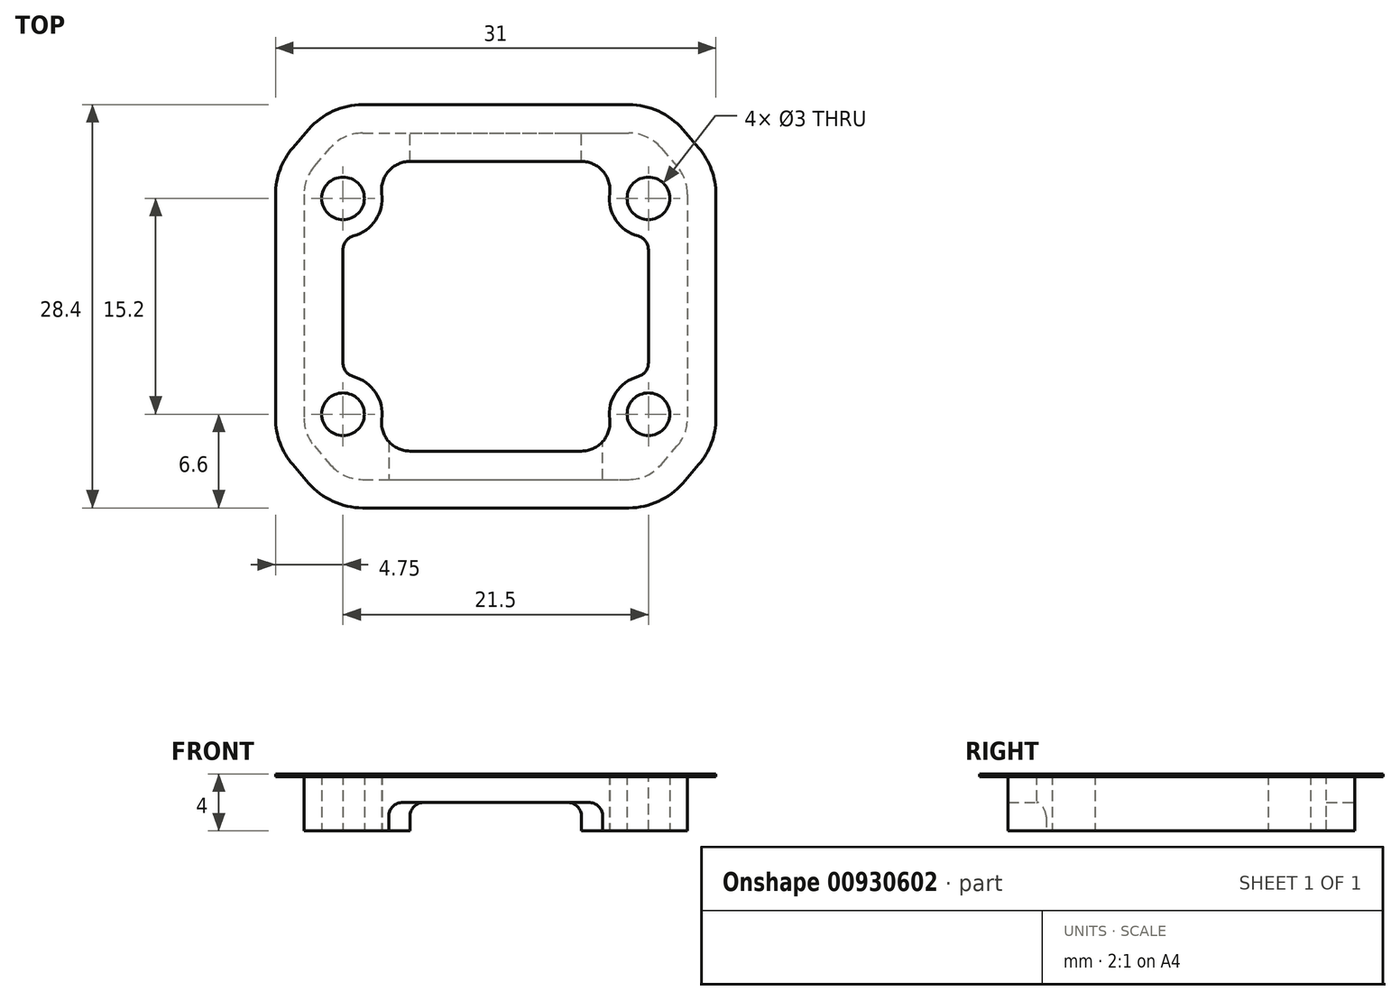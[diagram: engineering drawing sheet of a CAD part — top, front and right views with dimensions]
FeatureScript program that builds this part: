
annotation { "Feature Type Name" : "Feature", "Feature Type Description" : "" }
export const myFeature = defineFeature(function(context is Context, id is Id, definition is map)
    precondition{}
    {
        {
            var Q0;
            Q0=qCreatedBy(makeId("Top.planeOp"),FACE);
            var sketch = newSketch(context, id + "F0", { "sketchPlane" : qUnion([Q0])});
            skCircle(sketch, "E0", {"center": v(0, 0) * mm, "radius": 1.5 * mm});
            skCircle(sketch, "E1", {"center": v(0, 15.2) * mm, "radius": 1.5 * mm});
            skCircle(sketch, "E2", {"center": v(21.5, 15.2) * mm, "radius": 1.5 * mm});
            skCircle(sketch, "E3", {"center": v(21.5, 0) * mm, "radius": 1.5 * mm});
            skLineSegment(sketch, "E4", {"start": v(-2.75, 16.6) * mm, "end": v(-2.75, -1.4) * mm});
            skLineSegment(sketch, "E5", {"start": v(24.25, 16.6) * mm, "end": v(24.25, -1.4) * mm});
            skLineSegment(sketch, "E6", {"start": v(0.9, -2.6) * mm, "end": v(20.6, -2.6) * mm});
            skLineSegment(sketch, "E7", {"start": v(0.9, 17.8) * mm, "end": v(20.6, 17.8) * mm});
            skArc(sketch, "E8", {"start": v(0, 12.45) * mm, "mid": v(2.71, 14.75) * mm, "end": v(0.9, 17.8) * mm});
            skLineSegment(sketch, "E9", {"start": v(0, 12.45) * mm, "end": v(0, 2.75) * mm});
            skLineSegment(sketch, "E10", {"start": v(0, 19.8) * mm, "end": v(21.5, 19.8) * mm});
            skLineSegment(sketch, "E11", {"start": v(-2.75, 16.6) * mm, "end": v(0, 19.8) * mm});
            skLineSegment(sketch, "E12", {"start": v(21.5, 12.45) * mm, "end": v(21.5, 2.75) * mm});
            skArc(sketch, "E13", {"start": v(20.6, 17.8) * mm, "mid": v(18.79, 14.75) * mm, "end": v(21.5, 12.45) * mm});
            skLineSegment(sketch, "E14", {"start": v(21.5, 19.8) * mm, "end": v(24.25, 16.6) * mm});
            skLineSegment(sketch, "E15", {"start": v(0, -4.6) * mm, "end": v(21.5, -4.6) * mm});
            skLineSegment(sketch, "E16", {"start": v(21.5, -4.6) * mm, "end": v(24.25, -1.4) * mm});
            skLineSegment(sketch, "E17", {"start": v(-2.75, -1.4) * mm, "end": v(0, -4.6) * mm});
            skArc(sketch, "E18", {"start": v(0.9, -2.6) * mm, "mid": v(2.71, 0.45) * mm, "end": v(0, 2.75) * mm});
            skArc(sketch, "E19", {"start": v(21.5, 2.75) * mm, "mid": v(18.79, 0.45) * mm, "end": v(20.6, -2.6) * mm});
            skSolve(sketch);
        }
        {
            var Q0;
            Q0=qSketchRegion(id+"F0",true);
            extrude(context, id + "F1", {"entities" : qUnion([Q0]), "depth" : 4 * mm, "offsetDistance" : 25 * mm});
        }
        {
            var Q0;
            Q0=makeQuery(id+"F1.opExtrude","SWEPT_EDGE",EDGE,{"disambiguationData":[OSD([sQuery(id+"F0.wireOp",EDGE,"E7"),sQuery(id+"F0.wireOp",EDGE,"E8")])]});
            var Q1;
            Q1=makeQuery(id+"F1.opExtrude","SWEPT_EDGE",EDGE,{"disambiguationData":[OSD([sQuery(id+"F0.wireOp",EDGE,"E7"),sQuery(id+"F0.wireOp",EDGE,"E13")])]});
            var Q2;
            Q2=makeQuery(id+"F1.opExtrude","SWEPT_EDGE",EDGE,{"disambiguationData":[OSD([sQuery(id+"F0.wireOp",EDGE,"E6"),sQuery(id+"F0.wireOp",EDGE,"E18")])]});
            var Q3;
            Q3=makeQuery(id+"F1.opExtrude","SWEPT_EDGE",EDGE,{"disambiguationData":[OSD([sQuery(id+"F0.wireOp",EDGE,"E6"),sQuery(id+"F0.wireOp",EDGE,"E19")])]});
            fillet(context, id + "F2", {"entities" : qUnion([Q0, Q1, Q2, Q3]), "radius" : 2 * mm, "tangentPropagation" : true, "allowEdgeOverflow" : false});
        }
        {
            var Q0;
            Q0=makeQuery(id+"F1.opExtrude","SWEPT_EDGE",EDGE,{"disambiguationData":[OSD([sQuery(id+"F0.wireOp",EDGE,"E8"),sQuery(id+"F0.wireOp",EDGE,"E9")])]});
            var Q1;
            Q1=makeQuery(id+"F1.opExtrude","SWEPT_EDGE",EDGE,{"disambiguationData":[OSD([sQuery(id+"F0.wireOp",EDGE,"E9"),sQuery(id+"F0.wireOp",EDGE,"E18")])]});
            var Q2;
            Q2=makeQuery(id+"F1.opExtrude","SWEPT_EDGE",EDGE,{"disambiguationData":[OSD([sQuery(id+"F0.wireOp",EDGE,"E12"),sQuery(id+"F0.wireOp",EDGE,"E13")])]});
            var Q3;
            Q3=makeQuery(id+"F1.opExtrude","SWEPT_EDGE",EDGE,{"disambiguationData":[OSD([sQuery(id+"F0.wireOp",EDGE,"E12"),sQuery(id+"F0.wireOp",EDGE,"E19")])]});
            fillet(context, id + "F3", {"entities" : qUnion([Q0, Q1, Q2, Q3]), "radius" : 1 * mm, "tangentPropagation" : true, "allowEdgeOverflow" : false});
        }
        {
            var Q0;
            Q0=makeQuery(id+"F1.opExtrude","SWEPT_EDGE",EDGE,{"disambiguationData":[OSD([sQuery(id+"F0.wireOp",EDGE,"E15"),sQuery(id+"F0.wireOp",EDGE,"E17")])]});
            var Q1;
            Q1=makeQuery(id+"F1.opExtrude","SWEPT_EDGE",EDGE,{"disambiguationData":[OSD([sQuery(id+"F0.wireOp",EDGE,"E15"),sQuery(id+"F0.wireOp",EDGE,"E16")])]});
            var Q2;
            Q2=makeQuery(id+"F1.opExtrude","SWEPT_EDGE",EDGE,{"disambiguationData":[OSD([sQuery(id+"F0.wireOp",EDGE,"E5"),sQuery(id+"F0.wireOp",EDGE,"E16")])]});
            var Q3;
            Q3=makeQuery(id+"F1.opExtrude","SWEPT_EDGE",EDGE,{"disambiguationData":[OSD([sQuery(id+"F0.wireOp",EDGE,"E5"),sQuery(id+"F0.wireOp",EDGE,"E14")])]});
            var Q4;
            Q4=makeQuery(id+"F1.opExtrude","SWEPT_EDGE",EDGE,{"disambiguationData":[OSD([sQuery(id+"F0.wireOp",EDGE,"E10"),sQuery(id+"F0.wireOp",EDGE,"E14")])]});
            var Q5;
            Q5=makeQuery(id+"F1.opExtrude","SWEPT_EDGE",EDGE,{"disambiguationData":[OSD([sQuery(id+"F0.wireOp",EDGE,"E10"),sQuery(id+"F0.wireOp",EDGE,"E11")])]});
            var Q6;
            Q6=makeQuery(id+"F1.opExtrude","SWEPT_EDGE",EDGE,{"disambiguationData":[OSD([sQuery(id+"F0.wireOp",EDGE,"E4"),sQuery(id+"F0.wireOp",EDGE,"E11")])]});
            var Q7;
            Q7=makeQuery(id+"F1.opExtrude","SWEPT_EDGE",EDGE,{"disambiguationData":[OSD([sQuery(id+"F0.wireOp",EDGE,"E4"),sQuery(id+"F0.wireOp",EDGE,"E17")])]});
            fillet(context, id + "F4", {"entities" : qUnion([Q0, Q1, Q2, Q3, Q4, Q5, Q6, Q7]), "radius" : 3 * mm, "tangentPropagation" : true, "allowEdgeOverflow" : false});
        }
        {
            var Q0;
            Q0=makeQuery(id+"F1.opExtrude","CAP_FACE",FACE,{"disambiguationData":[OSD([sQuery(id+"F0.wireOp",EDGE,"E0"),sQuery(id+"F0.wireOp",EDGE,"E1"),sQuery(id+"F0.wireOp",EDGE,"E2"),sQuery(id+"F0.wireOp",EDGE,"E3"),sQuery(id+"F0.wireOp",EDGE,"E4"),sQuery(id+"F0.wireOp",EDGE,"E5"),sQuery(id+"F0.wireOp",EDGE,"E6"),sQuery(id+"F0.wireOp",EDGE,"E7"),sQuery(id+"F0.wireOp",EDGE,"E8"),sQuery(id+"F0.wireOp",EDGE,"E9"),sQuery(id+"F0.wireOp",EDGE,"E10"),sQuery(id+"F0.wireOp",EDGE,"E11"),sQuery(id+"F0.wireOp",EDGE,"E12"),sQuery(id+"F0.wireOp",EDGE,"E13"),sQuery(id+"F0.wireOp",EDGE,"E14"),sQuery(id+"F0.wireOp",EDGE,"E15"),sQuery(id+"F0.wireOp",EDGE,"E16"),sQuery(id+"F0.wireOp",EDGE,"E17"),sQuery(id+"F0.wireOp",EDGE,"E18"),sQuery(id+"F0.wireOp",EDGE,"E19")])],"isStart":true});
            var sketch = newSketch(context, id + "F5", { "sketchPlane" : qUnion([Q0])});
            skLineSegment(sketch, "E20.bottom", {"start": v(4.71, -17.8) * mm, "end": v(16.79, -17.8) * mm});
            skLineSegment(sketch, "E20.top", {"start": v(4.71, -19.8) * mm, "end": v(16.79, -19.8) * mm});
            skLineSegment(sketch, "E20.left", {"start": v(4.71, -17.8) * mm, "end": v(4.71, -19.8) * mm});
            skLineSegment(sketch, "E20.right", {"start": v(16.79, -17.8) * mm, "end": v(16.79, -19.8) * mm});
            skLineSegment(sketch, "E21", {"start": v(3.21, 1.92) * mm, "end": v(3.21, 4.6) * mm});
            skLineSegment(sketch, "E22", {"start": v(3.21, 4.6) * mm, "end": v(18.29, 4.6) * mm});
            skLineSegment(sketch, "E23", {"start": v(18.29, 4.6) * mm, "end": v(18.29, 1.92) * mm});
            skLineSegment(sketch, "E24", {"start": v(4.71, 2.6) * mm, "end": v(16.79, 2.6) * mm});
            skArc(sketch, "E25", {"start": v(4.71, 2.6) * mm, "mid": v(3.89, 2.42) * mm, "end": v(3.21, 1.92) * mm});
            skArc(sketch, "E26", {"start": v(18.29, 1.92) * mm, "mid": v(17.61, 2.42) * mm, "end": v(16.79, 2.6) * mm});
            skSolve(sketch);
        }
        {
            var Q0;
            Q0=qSketchRegion(id+"F5",true);
            extrude(context, id + "F6", {"entities" : qUnion([Q0]), "operationType" : NewBodyOperationType.REMOVE, "oppositeDirection" : true, "depth" : 2 * mm, "offsetDistance" : 25 * mm});
        }
        {
            var Q0;
            Q0=makeQuery(id+"F1.opExtrude","CAP_FACE",FACE,{"disambiguationData":[OSD([sQuery(id+"F0.wireOp",EDGE,"E0"),sQuery(id+"F0.wireOp",EDGE,"E1"),sQuery(id+"F0.wireOp",EDGE,"E2"),sQuery(id+"F0.wireOp",EDGE,"E3"),sQuery(id+"F0.wireOp",EDGE,"E4"),sQuery(id+"F0.wireOp",EDGE,"E5"),sQuery(id+"F0.wireOp",EDGE,"E6"),sQuery(id+"F0.wireOp",EDGE,"E7"),sQuery(id+"F0.wireOp",EDGE,"E8"),sQuery(id+"F0.wireOp",EDGE,"E9"),sQuery(id+"F0.wireOp",EDGE,"E10"),sQuery(id+"F0.wireOp",EDGE,"E11"),sQuery(id+"F0.wireOp",EDGE,"E12"),sQuery(id+"F0.wireOp",EDGE,"E13"),sQuery(id+"F0.wireOp",EDGE,"E14"),sQuery(id+"F0.wireOp",EDGE,"E15"),sQuery(id+"F0.wireOp",EDGE,"E16"),sQuery(id+"F0.wireOp",EDGE,"E17"),sQuery(id+"F0.wireOp",EDGE,"E18"),sQuery(id+"F0.wireOp",EDGE,"E19")])],"isStart":false});
            var sketch = newSketch(context, id + "F7", { "sketchPlane" : qUnion([Q0])});
            skLineSegment(sketch, "E27", {"start": v(-2.75, 15.5) * mm, "end": v(-2.75, -0.3) * mm});
            skLineSegment(sketch, "E28", {"start": v(-2.02, -2.25) * mm, "end": v(-0.9, -3.56) * mm});
            skLineSegment(sketch, "E29", {"start": v(1.38, -4.6) * mm, "end": v(20.12, -4.6) * mm});
            skLineSegment(sketch, "E30", {"start": v(22.4, -3.56) * mm, "end": v(23.52, -2.25) * mm});
            skLineSegment(sketch, "E31", {"start": v(24.25, -0.3) * mm, "end": v(24.25, 15.5) * mm});
            skLineSegment(sketch, "E32", {"start": v(23.52, 17.45) * mm, "end": v(22.4, 18.76) * mm});
            skLineSegment(sketch, "E33", {"start": v(20.12, 19.8) * mm, "end": v(1.38, 19.8) * mm});
            skLineSegment(sketch, "E34", {"start": v(-0.9, 18.76) * mm, "end": v(-2.02, 17.45) * mm});
            skArc(sketch, "E35", {"start": v(-2.02, 17.45) * mm, "mid": v(-2.56, 16.53) * mm, "end": v(-2.75, 15.5) * mm});
            skArc(sketch, "E36", {"start": v(1.38, 19.8) * mm, "mid": v(0.13, 19.53) * mm, "end": v(-0.9, 18.76) * mm});
            skArc(sketch, "E37", {"start": v(22.4, 18.76) * mm, "mid": v(21.37, 19.53) * mm, "end": v(20.12, 19.8) * mm});
            skArc(sketch, "E38", {"start": v(24.25, 15.5) * mm, "mid": v(24.06, 16.53) * mm, "end": v(23.52, 17.45) * mm});
            skArc(sketch, "E39", {"start": v(23.52, -2.25) * mm, "mid": v(24.06, -1.33) * mm, "end": v(24.25, -0.3) * mm});
            skArc(sketch, "E40", {"start": v(20.12, -4.6) * mm, "mid": v(21.37, -4.33) * mm, "end": v(22.4, -3.56) * mm});
            skArc(sketch, "E41", {"start": v(-0.9, -3.56) * mm, "mid": v(0.13, -4.33) * mm, "end": v(1.38, -4.6) * mm});
            skArc(sketch, "E42", {"start": v(-2.75, -0.3) * mm, "mid": v(-2.56, -1.33) * mm, "end": v(-2.02, -2.25) * mm});
            skLineSegment(sketch, "E43", {"start": v(-4.75, 15.5) * mm, "end": v(-4.75, -0.3) * mm});
            skLineSegment(sketch, "E44", {"start": v(-3.54, 18.75) * mm, "end": v(-2.41, 20.06) * mm});
            skLineSegment(sketch, "E45", {"start": v(1.38, 21.8) * mm, "end": v(20.12, 21.8) * mm});
            skLineSegment(sketch, "E46", {"start": v(23.91, 20.06) * mm, "end": v(25.04, 18.75) * mm});
            skLineSegment(sketch, "E47", {"start": v(26.25, 15.5) * mm, "end": v(26.25, -0.3) * mm});
            skLineSegment(sketch, "E48", {"start": v(25.04, -3.55) * mm, "end": v(23.91, -4.86) * mm});
            skLineSegment(sketch, "E49", {"start": v(-3.54, -3.55) * mm, "end": v(-2.41, -4.86) * mm});
            skLineSegment(sketch, "E50", {"start": v(1.38, -6.6) * mm, "end": v(20.12, -6.6) * mm});
            skArc(sketch, "E51", {"start": v(20.12, -6.6) * mm, "mid": v(22.2, -6.14) * mm, "end": v(23.91, -4.86) * mm});
            skArc(sketch, "E52", {"start": v(25.04, -3.55) * mm, "mid": v(25.94, -2.03) * mm, "end": v(26.25, -0.3) * mm});
            skArc(sketch, "E53", {"start": v(26.25, 15.5) * mm, "mid": v(25.94, 17.23) * mm, "end": v(25.04, 18.75) * mm});
            skArc(sketch, "E54", {"start": v(23.91, 20.06) * mm, "mid": v(22.2, 21.34) * mm, "end": v(20.12, 21.8) * mm});
            skArc(sketch, "E55", {"start": v(1.38, 21.8) * mm, "mid": v(-0.7, 21.34) * mm, "end": v(-2.41, 20.06) * mm});
            skArc(sketch, "E56", {"start": v(-3.54, 18.75) * mm, "mid": v(-4.44, 17.23) * mm, "end": v(-4.75, 15.5) * mm});
            skArc(sketch, "E57", {"start": v(-4.75, -0.3) * mm, "mid": v(-4.44, -2.03) * mm, "end": v(-3.54, -3.55) * mm});
            skArc(sketch, "E58", {"start": v(-2.41, -4.86) * mm, "mid": v(-0.7, -6.14) * mm, "end": v(1.38, -6.6) * mm});
            skSolve(sketch);
        }
        {
            var Q0;
            Q0=qSketchRegion(id+"F7",true);
            extrude(context, id + "F8", {"entities" : qUnion([Q0]), "operationType" : NewBodyOperationType.ADD, "oppositeDirection" : true, "depth" : 0.2 * mm, "offsetDistance" : 25 * mm});
        }
        {
            var Q0;
            Q0=makeQuery(id+"F6.boolean.opBoolean","COPY",EDGE,{"derivedFrom":makeQuery(id+"F6.opExtrude","CAP_EDGE",EDGE,{"disambiguationData":[OSD([sQuery(id+"F5.wireOp",EDGE,"E21")])],"isStart":false})});
            var Q1;
            Q1=makeQuery(id+"F6.boolean.opBoolean","COPY",EDGE,{"derivedFrom":makeQuery(id+"F6.opExtrude","CAP_EDGE",EDGE,{"disambiguationData":[OSD([sQuery(id+"F5.wireOp",EDGE,"E23")])],"isStart":false})});
            var Q2;
            Q2=makeQuery(id+"F6.boolean.opBoolean","COPY",EDGE,{"derivedFrom":makeQuery(id+"F6.opExtrude","CAP_EDGE",EDGE,{"disambiguationData":[OSD([sQuery(id+"F5.wireOp",EDGE,"E20.right")])],"isStart":false})});
            var Q3;
            Q3=makeQuery(id+"F6.boolean.opBoolean","COPY",EDGE,{"derivedFrom":makeQuery(id+"F6.opExtrude","CAP_EDGE",EDGE,{"disambiguationData":[OSD([sQuery(id+"F5.wireOp",EDGE,"E20.left")])],"isStart":false})});
            fillet(context, id + "F9", {"entities" : qUnion([Q0, Q1, Q2, Q3]), "radius" : 1 * mm, "tangentPropagation" : true, "allowEdgeOverflow" : false});
        }
    });
